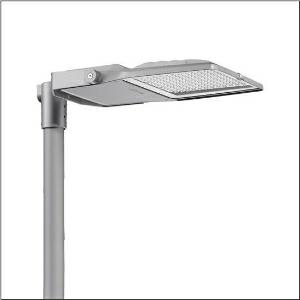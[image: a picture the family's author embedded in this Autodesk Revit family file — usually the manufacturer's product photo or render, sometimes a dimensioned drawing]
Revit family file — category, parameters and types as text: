
# Revit family: floodlight_fl_21_midi___pl61_5xa7786f4c3a_8fd3
name_source: partatom
category: Lighting Fixtures
units: mm (PartAtom-declared; Revit-internal decimal feet)

## family parameters
Cut with Voids When Loaded = No
Host = Face
Light Source = No
Part Type = Normal
Room Calculation Point = No
Round Connector Dimension = Use Diameter
Shared = No

## types (1)
- --- (1 x LED, 36640 lm, 271.6 W, 4000K)
    Apparent Load = 272 VA
    CIE Flux Codes = 33 65 98 100 100
    Color Rendering = 70
    Color Temperature = 4000K
    Default Elevation = 1800 mm
    Description = Floodlight FL 21 midi, floodlight, primary light control with lens, of PMMA, primary optical cover: protective disc, of toughened safety glass, transparent, light distribution: PL61, light emission: direct distribution, installation type: surface-mounted, LED, High Power LED, rated luminous flux: 36.640lm, luminous efficacy: 135lm/W, light colour: 740, colour temperature: 4000K, control gear: Smart Interface (Zhaga)D4i, control: overheat protection, constant luminous flux control, time-dependent luminous flux control, flexible luminous flux parameterisation, pre-setting: logarithmic dimming characteristic, with terminal, 6-pole, mains connection: 220..240V, AC, 50/60Hz, start of lifetime: 272W, end of service life: 287W, reduction: 123W, mast bracket, of diecast aluminium, powder-coated, Siteco® metallic grey (DB 702S), corrosivity category C5 mid according to DIN EN ISO 12944, suitable for swimming pools, chlorine-resistant, sealing non-destructively replaceable, mast bracket, of steel, galvanised, powder-coated, Siteco® metallic grey (DB 702S), Smart Interface below and above, protection rating (complete): IP66, insulation class (complete): insulation class II (safety insulation), certification: CE, ENEC, VDE, protection symbol: D, impact resistance: IK08, permissible operating ambient temperature: -40..+40°C, permissible operating ambient temperature for outdoor applications: -40..+50°C, standard: DIN EN 12944, LABS conformity tested according to VDMA 24364:2018-05, packaging unit: 1 piece

Light Distribution: PL61
    Height = 76 mm
    Lamp = 1 x LED
    Lamp Light Flux = 36640 lm
    Lamp Power = 271.6 W
    Lamp count = 1
    Length = 657 mm
    Luminous efficacy = 135 lm/W
    Manufacturer = Siteco
    ModVariant = No
    Model = 5XA7786F4C3A
    Number of Poles = 1
    OnlyDefault = Yes
    Power Factor = 1
    Product Name = Floodlight FL 21 midi | PL61
    Product group = floodlight | pylon annexe
    ProductGroupID = 6201
    Protection Class = Protection class II
    Protection Degree = IP 66
    RLX_Detail_Level = 1
    RLX_Emergency_Light_Flux = 0 lm
    RLX_Emergency_Type = 0
    RLX_Emergency_Type_DB = No
    RlxData = <blob elided: 104589 chars, md5=a775139f>
    Socket = socket
    Standby Power = 0 W
    System Light Flux = 36640 lm
    System Power = 272 W
    Type Comments = factory setting: luminous flux: 100 % | dim-lin: 254 | 620 mA
    Type Image = l_1007123.jpg
    URL = http://relux.com
    VarID = @adj_111987
    Voltage = 0 V
    Weight = 0.00 kg
    Width = 442 mm

## geometry (parser evidence)
native form markers: Blend x4, Sweep x11
no freeform markers — native parametric forms only
